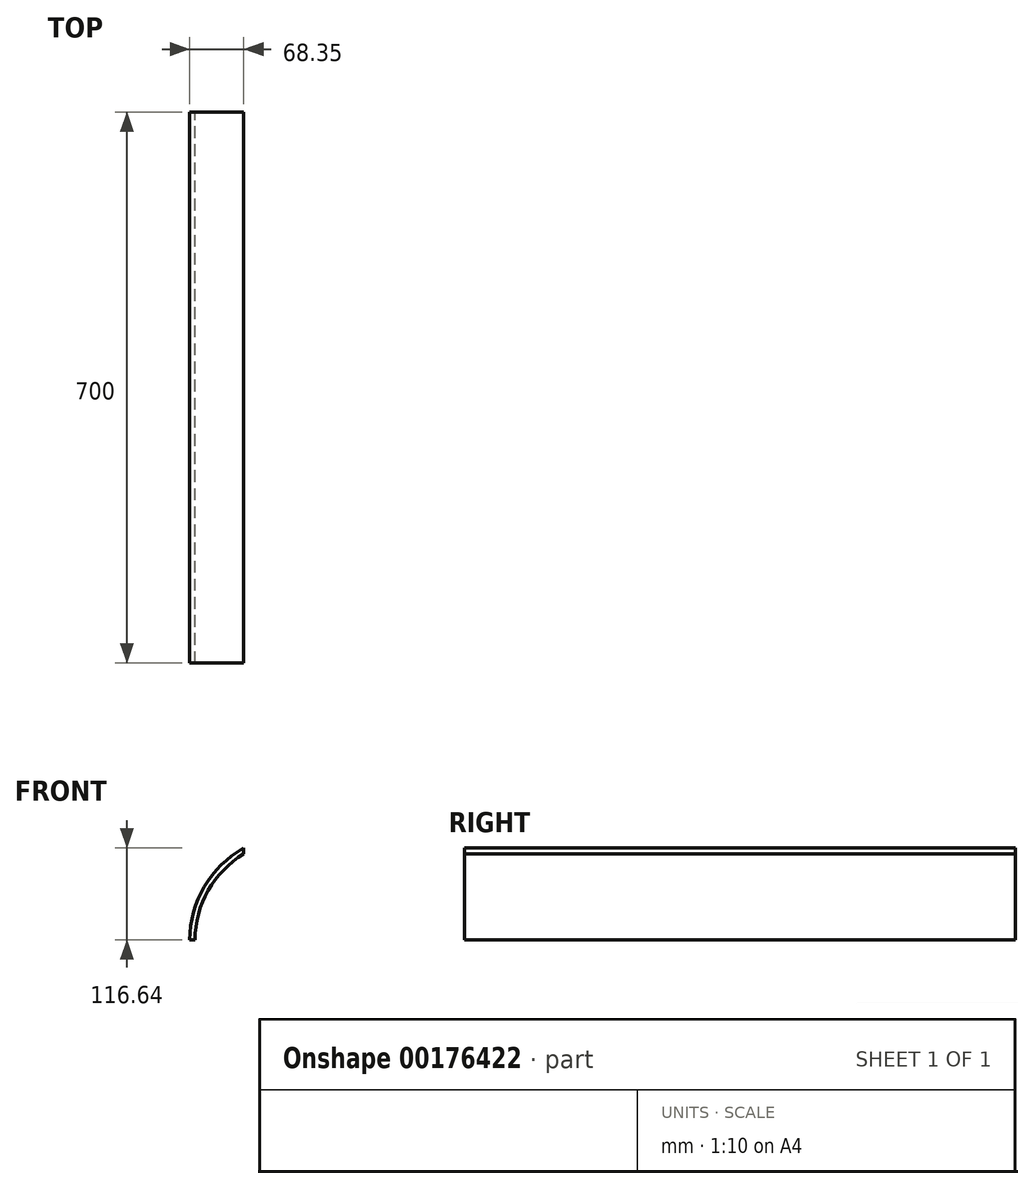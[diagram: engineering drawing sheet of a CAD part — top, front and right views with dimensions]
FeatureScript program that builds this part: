
annotation { "Feature Type Name" : "Feature", "Feature Type Description" : "" }
export const myFeature = defineFeature(function(context is Context, id is Id, definition is map)
    precondition{}
    {
        {
            var Q0;
            Q0=qCreatedBy(makeId("Front.planeOp"),FACE);
            var sketch = newSketch(context, id + "F0", { "sketchPlane" : qUnion([Q0])});
            skArc(sketch, "E0", {"start": v(0, 0) * mm, "mid": v(-50, -49.04) * mm, "end": v(-68.35, -116.64) * mm});
            skLineSegment(sketch, "E1", {"start": v(-61.75, -116.64) * mm, "end": v(-68.35, -116.64) * mm});
            skPoint(sketch, "E2", {"position": v(-68.35, -116.64) * mm});
            skArc(sketch, "E3", {"start": v(0, -7.63) * mm, "mid": v(-45.24, -54) * mm, "end": v(-61.75, -116.64) * mm});
            skLineSegment(sketch, "E4", {"start": v(0, 0) * mm, "end": v(0, -7.63) * mm});
            skSolve(sketch);
        }
        {
            var Q0;
            Q0=makeQuery(id+"F0.imprint","IMPRINT",FACE,{"disambiguationData":[TD([[makeQuery(id+"F0.imprint","IMPRINT",EDGE,{"derivedFrom":sQuery(id+"F0.wireOp",EDGE,"E0")}),1.0]])]});
            extrude(context, id + "F1", {"entities" : qUnion([Q0]), "depth" : 500 * mm, "hasSecondDirection" : true, "secondDirectionOppositeDirection" : true, "secondDirectionDepth" : 200 * mm});
        }
    });
